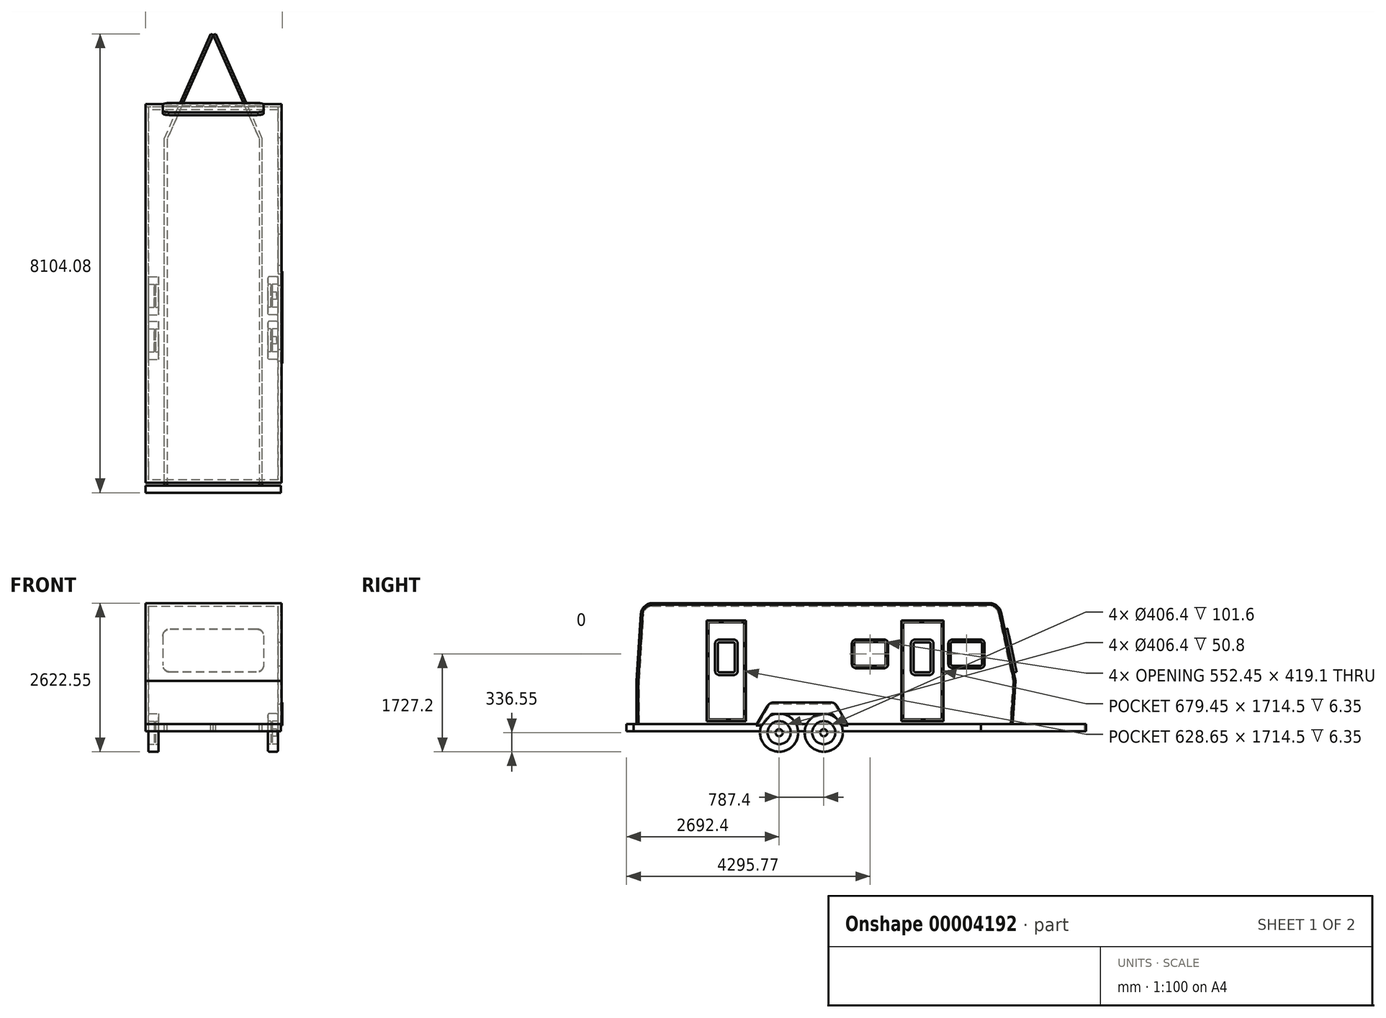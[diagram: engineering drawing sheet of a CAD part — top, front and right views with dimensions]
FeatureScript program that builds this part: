
annotation { "Feature Type Name" : "Feature", "Feature Type Description" : "" }
export const myFeature = defineFeature(function(context is Context, id is Id, definition is map)
    precondition{}
    {
        {
            var Q0;
            Q0=qCreatedBy(makeId("Right.planeOp"),FACE);
            var sketch = newSketch(context, id + "F0", { "sketchPlane" : qUnion([Q0])});
            skLineSegment(sketch, "E0", {"start": v(3587.75, 0) * mm, "end": v(-3048, 0) * mm});
            skLineSegment(sketch, "E1", {"start": v(-3048, 0) * mm, "end": v(-3048, 762) * mm});
            skLineSegment(sketch, "E2", {"start": v(-3048, 762) * mm, "end": v(-2971.8, 1943.48) * mm});
            skArc(sketch, "E3", {"start": v(-2971.8, 1943.48) * mm, "mid": v(-2908, 2078.64) * mm, "end": v(-2769.02, 2133.6) * mm});
            skLineSegment(sketch, "E4", {"start": v(-2769.02, 2133.6) * mm, "end": v(3181.35, 2133.6) * mm});
            skArc(sketch, "E5", {"start": v(3181.35, 2133.6) * mm, "mid": v(3309.16, 2088.37) * mm, "end": v(3380.07, 1972.82) * mm});
            skLineSegment(sketch, "E6", {"start": v(3380.07, 1972.82) * mm, "end": v(3638.55, 762) * mm});
            skLineSegment(sketch, "E7", {"start": v(3638.55, 762) * mm, "end": v(3587.75, 0) * mm});
            skLineSegment(sketch, "E8", {"start": v(2368.55, 0) * mm, "end": v(2368.55, 1879.6) * mm, "construction": true});
            skLineSegment(sketch, "E9", {"start": v(2368.55, 1879.6) * mm, "end": v(1689.1, 1879.6) * mm, "construction": true});
            skLineSegment(sketch, "E10", {"start": v(1689.1, 1879.6) * mm, "end": v(1689.1, 0) * mm, "construction": true});
            skLineSegment(sketch, "E11", {"start": v(-1149.35, 0) * mm, "end": v(-1149.35, 1879.6) * mm, "construction": true});
            skLineSegment(sketch, "E12", {"start": v(-1149.35, 1879.6) * mm, "end": v(-1778, 1879.6) * mm, "construction": true});
            skLineSegment(sketch, "E13", {"start": v(-1778, 1879.6) * mm, "end": v(-1778, 0) * mm, "construction": true});
            skLineSegment(sketch, "E14", {"start": v(-3048, 762) * mm, "end": v(-3048, 2133.6) * mm, "construction": true});
            skSolve(sketch);
        }
        {
            var Q0;
            Q0 = qSketchRegion(id + "F0", true);
            extrude(context, id + "F1", {"entities" : qUnion([Q0]), "endBound" : BoundingType.SYMMETRIC, "depth" : 2387.6 * mm});
        }
        {
            var Q0;
            Q0=makeQuery(id+"F1.opExtrude","SWEPT_FACE",FACE,{"disambiguationData":[OSD([sQuery(id+"F0.wireOp",EDGE,"E0")])]});
            shell(context, id + "F2", {"entities" : qUnion([Q0]), "thickness" : 50.8 * mm});
        }
        {
            var Q0;
            Q0=makeQuery(id+"F1.opExtrude","CAP_FACE",FACE,{"disambiguationData":[OSD([sQuery(id+"F0.wireOp",EDGE,"E0"),sQuery(id+"F0.wireOp",EDGE,"E1"),sQuery(id+"F0.wireOp",EDGE,"E2"),sQuery(id+"F0.wireOp",EDGE,"E3"),sQuery(id+"F0.wireOp",EDGE,"E4"),sQuery(id+"F0.wireOp",EDGE,"E5"),sQuery(id+"F0.wireOp",EDGE,"E6"),sQuery(id+"F0.wireOp",EDGE,"E7")])],"isStart":false});
            var sketch = newSketch(context, id + "F3", { "sketchPlane" : qUnion([Q0])});
            skLineSegment(sketch, "E15.bottom", {"start": v(2368.55, 1828.8) * mm, "end": v(1625.6, 1828.8) * mm});
            skLineSegment(sketch, "E15.top", {"start": v(2368.55, 50.8) * mm, "end": v(1625.6, 50.8) * mm});
            skLineSegment(sketch, "E15.left", {"start": v(2368.55, 1828.8) * mm, "end": v(2368.55, 50.8) * mm});
            skLineSegment(sketch, "E15.right", {"start": v(1625.6, 1828.8) * mm, "end": v(1625.6, 50.8) * mm});
            skLineSegment(sketch, "E16.bottom", {"start": v(-1117.6, 1828.8) * mm, "end": v(-1809.75, 1828.8) * mm});
            skLineSegment(sketch, "E16.top", {"start": v(-1117.6, 50.8) * mm, "end": v(-1809.75, 50.8) * mm});
            skLineSegment(sketch, "E16.left", {"start": v(-1117.6, 1828.8) * mm, "end": v(-1117.6, 50.8) * mm});
            skLineSegment(sketch, "E16.right", {"start": v(-1809.75, 1828.8) * mm, "end": v(-1809.75, 50.8) * mm});
            skLineSegment(sketch, "E17.bottom", {"start": v(-1149.35, 1797.05) * mm, "end": v(-1778, 1797.05) * mm});
            skLineSegment(sketch, "E17.top", {"start": v(-1149.35, 82.55) * mm, "end": v(-1778, 82.55) * mm});
            skLineSegment(sketch, "E17.left", {"start": v(-1149.35, 1797.05) * mm, "end": v(-1149.35, 82.55) * mm});
            skLineSegment(sketch, "E17.right", {"start": v(-1778, 1797.05) * mm, "end": v(-1778, 82.55) * mm});
            skLineSegment(sketch, "E18.bottom", {"start": v(2336.8, 1797.05) * mm, "end": v(1657.35, 1797.05) * mm});
            skLineSegment(sketch, "E18.top", {"start": v(2336.8, 82.55) * mm, "end": v(1657.35, 82.55) * mm});
            skLineSegment(sketch, "E18.left", {"start": v(2336.8, 1797.05) * mm, "end": v(2336.8, 82.55) * mm});
            skLineSegment(sketch, "E18.right", {"start": v(1657.35, 1797.05) * mm, "end": v(1657.35, 82.55) * mm});
            skSolve(sketch);
        }
        {
            var Q0;
            Q0 = qSketchRegion(id + "F3", true);
            extrude(context, id + "F4", {"entities" : qUnion([Q0]), "operationType" : NewBodyOperationType.ADD, "depth" : 6.35 * mm});
        }
        {
            var Q0;
            Q0=makeQuery(id+"F1.opExtrude","CAP_FACE",FACE,{"disambiguationData":[OSD([sQuery(id+"F0.wireOp",EDGE,"E0"),sQuery(id+"F0.wireOp",EDGE,"E1"),sQuery(id+"F0.wireOp",EDGE,"E2"),sQuery(id+"F0.wireOp",EDGE,"E3"),sQuery(id+"F0.wireOp",EDGE,"E4"),sQuery(id+"F0.wireOp",EDGE,"E5"),sQuery(id+"F0.wireOp",EDGE,"E6"),sQuery(id+"F0.wireOp",EDGE,"E7")])],"isStart":false});
            var sketch = newSketch(context, id + "F5", { "sketchPlane" : qUnion([Q0])});
            skLineSegment(sketch, "E19", {"start": v(-1263.65, 939.8) * mm, "end": v(-1263.65, 1416.05) * mm});
            skArc(sketch, "E20", {"start": v(-1263.65, 1416.05) * mm, "mid": v(-1285.97, 1469.93) * mm, "end": v(-1339.85, 1492.25) * mm});
            skLineSegment(sketch, "E21", {"start": v(-1339.85, 1492.25) * mm, "end": v(-1587.5, 1492.25) * mm});
            skArc(sketch, "E22", {"start": v(-1587.5, 1492.25) * mm, "mid": v(-1641.38, 1469.93) * mm, "end": v(-1663.7, 1416.05) * mm});
            skLineSegment(sketch, "E23", {"start": v(-1663.7, 1416.05) * mm, "end": v(-1663.7, 939.8) * mm});
            skArc(sketch, "E24", {"start": v(-1663.7, 939.8) * mm, "mid": v(-1641.38, 885.92) * mm, "end": v(-1587.5, 863.6) * mm});
            skLineSegment(sketch, "E25", {"start": v(-1587.5, 863.6) * mm, "end": v(-1339.85, 863.6) * mm});
            skArc(sketch, "E26", {"start": v(-1339.85, 863.6) * mm, "mid": v(-1285.97, 885.92) * mm, "end": v(-1263.65, 939.8) * mm});
            skArc(sketch, "E27.0", {"start": v(-1314.45, 1416.05) * mm, "mid": v(-1321.89, 1434.01) * mm, "end": v(-1339.85, 1441.45) * mm});
            skLineSegment(sketch, "E27.1", {"start": v(-1314.45, 939.8) * mm, "end": v(-1314.45, 1416.05) * mm});
            skLineSegment(sketch, "E27.2", {"start": v(-1339.85, 1441.45) * mm, "end": v(-1587.5, 1441.45) * mm});
            skArc(sketch, "E27.3", {"start": v(-1339.85, 914.4) * mm, "mid": v(-1321.89, 921.84) * mm, "end": v(-1314.45, 939.8) * mm});
            skArc(sketch, "E27.4", {"start": v(-1587.5, 1441.45) * mm, "mid": v(-1605.46, 1434.01) * mm, "end": v(-1612.9, 1416.05) * mm});
            skLineSegment(sketch, "E27.5", {"start": v(-1612.9, 1416.05) * mm, "end": v(-1612.9, 939.8) * mm});
            skArc(sketch, "E27.6", {"start": v(-1612.9, 939.8) * mm, "mid": v(-1605.46, 921.84) * mm, "end": v(-1587.5, 914.4) * mm});
            skLineSegment(sketch, "E27.7", {"start": v(-1587.5, 914.4) * mm, "end": v(-1339.85, 914.4) * mm});
            skSolve(sketch);
        }
        {
            var Q0;
            Q0 = qSketchRegion(id + "F5", true);
            extrude(context, id + "F6", {"entities" : qUnion([Q0]), "depth" : 12.7 * mm});
        }
        {
            var Q0;
            Q0=makeQuery(id+"F6.opExtrude","SWEPT_BODY",BODY,{"disambiguationData":[OSD([sQuery(id+"F5.wireOp",EDGE,"E19"),sQuery(id+"F5.wireOp",EDGE,"E20"),sQuery(id+"F5.wireOp",EDGE,"E21"),sQuery(id+"F5.wireOp",EDGE,"E22"),sQuery(id+"F5.wireOp",EDGE,"E23"),sQuery(id+"F5.wireOp",EDGE,"E24"),sQuery(id+"F5.wireOp",EDGE,"E25"),sQuery(id+"F5.wireOp",EDGE,"E26"),sQuery(id+"F5.wireOp",EDGE,"E27.0"),sQuery(id+"F5.wireOp",EDGE,"E27.1"),sQuery(id+"F5.wireOp",EDGE,"E27.2"),sQuery(id+"F5.wireOp",EDGE,"E27.3"),sQuery(id+"F5.wireOp",EDGE,"E27.4"),sQuery(id+"F5.wireOp",EDGE,"E27.5"),sQuery(id+"F5.wireOp",EDGE,"E27.6"),sQuery(id+"F5.wireOp",EDGE,"E27.7")])]});
            var Q1;
            Q1=makeQuery(id+"F1.opExtrude","CAP_EDGE",EDGE,{"disambiguationData":[OSD([sQuery(id+"F0.wireOp",EDGE,"E4")])],"isStart":false});
            transform(context, id + "F7", {"entities" : qUnion([Q0]), "transformType" : TransformType.TRANSLATION_DISTANCE, "transformDirection" : qUnion([Q1]), "distance" : 3454.4 * mm, "makeCopy" : true});
        }
        {
            var Q0;
            Q0=makeQuery(id+"F1.opExtrude","CAP_FACE",FACE,{"disambiguationData":[OSD([sQuery(id+"F0.wireOp",EDGE,"E0"),sQuery(id+"F0.wireOp",EDGE,"E1"),sQuery(id+"F0.wireOp",EDGE,"E2"),sQuery(id+"F0.wireOp",EDGE,"E3"),sQuery(id+"F0.wireOp",EDGE,"E4"),sQuery(id+"F0.wireOp",EDGE,"E5"),sQuery(id+"F0.wireOp",EDGE,"E6"),sQuery(id+"F0.wireOp",EDGE,"E7")])],"isStart":false});
            var sketch = newSketch(context, id + "F8", { "sketchPlane" : qUnion([Q0])});
            skLineSegment(sketch, "E28", {"start": v(3016.25, 1492.25) * mm, "end": v(2527.3, 1492.25) * mm});
            skArc(sketch, "E29", {"start": v(2527.3, 1492.25) * mm, "mid": v(2473.42, 1469.93) * mm, "end": v(2451.1, 1416.05) * mm});
            skLineSegment(sketch, "E30", {"start": v(2451.1, 1416.05) * mm, "end": v(2451.1, 1060.45) * mm});
            skArc(sketch, "E31", {"start": v(2451.1, 1060.45) * mm, "mid": v(2473.42, 1006.57) * mm, "end": v(2527.3, 984.25) * mm});
            skLineSegment(sketch, "E32", {"start": v(2527.3, 984.25) * mm, "end": v(3016.25, 984.25) * mm});
            skArc(sketch, "E33", {"start": v(3016.25, 984.25) * mm, "mid": v(3070.13, 1006.57) * mm, "end": v(3092.45, 1060.45) * mm});
            skLineSegment(sketch, "E34", {"start": v(3092.45, 1060.45) * mm, "end": v(3092.45, 1416.05) * mm});
            skArc(sketch, "E35", {"start": v(3092.45, 1416.05) * mm, "mid": v(3070.13, 1469.93) * mm, "end": v(3016.25, 1492.25) * mm});
            skArc(sketch, "E36.0", {"start": v(3048, 1416.05) * mm, "mid": v(3038.7, 1438.5) * mm, "end": v(3016.25, 1447.8) * mm});
            skLineSegment(sketch, "E36.1", {"start": v(3048, 1060.45) * mm, "end": v(3048, 1416.05) * mm});
            skLineSegment(sketch, "E36.2", {"start": v(3016.25, 1447.8) * mm, "end": v(2527.3, 1447.8) * mm});
            skArc(sketch, "E36.3", {"start": v(3016.25, 1028.7) * mm, "mid": v(3038.7, 1038) * mm, "end": v(3048, 1060.45) * mm});
            skArc(sketch, "E36.4", {"start": v(2527.3, 1447.8) * mm, "mid": v(2504.85, 1438.5) * mm, "end": v(2495.55, 1416.05) * mm});
            skLineSegment(sketch, "E36.5", {"start": v(2495.55, 1416.05) * mm, "end": v(2495.55, 1060.45) * mm});
            skArc(sketch, "E36.6", {"start": v(2495.55, 1060.45) * mm, "mid": v(2504.85, 1038) * mm, "end": v(2527.3, 1028.7) * mm});
            skLineSegment(sketch, "E36.7", {"start": v(2527.3, 1028.7) * mm, "end": v(3016.25, 1028.7) * mm});
            skSolve(sketch);
        }
        {
            var Q0;
            Q0 = qSketchRegion(id + "F8", true);
            extrude(context, id + "F9", {"entities" : qUnion([Q0]), "depth" : 6.35 * mm});
        }
        {
            var Q0;
            Q0=makeQuery(id+"F9.opExtrude","SWEPT_BODY",BODY,{"disambiguationData":[OSD([sQuery(id+"F8.wireOp",EDGE,"E28"),sQuery(id+"F8.wireOp",EDGE,"E29"),sQuery(id+"F8.wireOp",EDGE,"E30"),sQuery(id+"F8.wireOp",EDGE,"E31"),sQuery(id+"F8.wireOp",EDGE,"E32"),sQuery(id+"F8.wireOp",EDGE,"E33"),sQuery(id+"F8.wireOp",EDGE,"E34"),sQuery(id+"F8.wireOp",EDGE,"E35"),sQuery(id+"F8.wireOp",EDGE,"E36.0"),sQuery(id+"F8.wireOp",EDGE,"E36.1"),sQuery(id+"F8.wireOp",EDGE,"E36.2"),sQuery(id+"F8.wireOp",EDGE,"E36.3"),sQuery(id+"F8.wireOp",EDGE,"E36.4"),sQuery(id+"F8.wireOp",EDGE,"E36.5"),sQuery(id+"F8.wireOp",EDGE,"E36.6"),sQuery(id+"F8.wireOp",EDGE,"E36.7")])]});
            transform(context, id + "F10", {"entities" : qUnion([Q0]), "transformType" : TransformType.TRANSLATION_3D, "dx" : 0 * mm, "dy" : -1701.8 * mm, "dz" : 0 * mm, "makeCopy" : true});
        }
        {
            var Q0;
            Q0=makeQuery(id+"F1.opExtrude","CAP_FACE",FACE,{"disambiguationData":[OSD([sQuery(id+"F0.wireOp",EDGE,"E0"),sQuery(id+"F0.wireOp",EDGE,"E1"),sQuery(id+"F0.wireOp",EDGE,"E2"),sQuery(id+"F0.wireOp",EDGE,"E3"),sQuery(id+"F0.wireOp",EDGE,"E4"),sQuery(id+"F0.wireOp",EDGE,"E5"),sQuery(id+"F0.wireOp",EDGE,"E6"),sQuery(id+"F0.wireOp",EDGE,"E7")])],"isStart":false});
            var sketch = newSketch(context, id + "F11", { "sketchPlane" : qUnion([Q0])});
            skLineSegment(sketch, "E37", {"start": v(1314.45, 1447.8) * mm, "end": v(825.5, 1447.8) * mm});
            skArc(sketch, "E38", {"start": v(825.5, 1447.8) * mm, "mid": v(803.05, 1438.5) * mm, "end": v(793.75, 1416.05) * mm});
            skLineSegment(sketch, "E39", {"start": v(793.75, 1416.05) * mm, "end": v(793.75, 1060.45) * mm});
            skArc(sketch, "E40", {"start": v(793.75, 1060.45) * mm, "mid": v(803.05, 1038) * mm, "end": v(825.5, 1028.7) * mm});
            skLineSegment(sketch, "E41", {"start": v(825.5, 1028.7) * mm, "end": v(1314.45, 1028.7) * mm});
            skArc(sketch, "E42", {"start": v(1314.45, 1447.8) * mm, "mid": v(1336.9, 1438.5) * mm, "end": v(1346.2, 1416.05) * mm});
            skLineSegment(sketch, "E43", {"start": v(1346.2, 1416.05) * mm, "end": v(1346.2, 1060.45) * mm});
            skArc(sketch, "E44", {"start": v(1346.2, 1060.45) * mm, "mid": v(1336.9, 1038) * mm, "end": v(1314.45, 1028.7) * mm});
            skSolve(sketch);
        }
        {
            var Q0;
            Q0 = qSketchRegion(id + "F11", true);
            extrude(context, id + "F12", {"entities" : qUnion([Q0]), "operationType" : NewBodyOperationType.REMOVE, "oppositeDirection" : true, "depth" : 50.8 * mm});
        }
        {
            var Q0;
            Q0=qCreatedBy(makeId("Right.planeOp"),FACE);
            cPlane(context, id + "F13", {"entities" : qUnion([Q0]), "cplaneType" : CPlaneType.OFFSET, "offset" : 965.2 * mm, "width" : 152.4 * mm, "height" : 152.4 * mm});
        }
        {
            var Q0;
            Q0=qCreatedBy(id+"F13.planeOp",FACE);
            var sketch = newSketch(context, id + "F14", { "sketchPlane" : qUnion([Q0])});
            skCircle(sketch, "E45", {"center": v(-533.4, -152.4) * mm, "radius": 336.55 * mm});
            skCircle(sketch, "E46", {"center": v(-533.4, -152.4) * mm, "radius": 203.2 * mm});
            skCircle(sketch, "E47", {"center": v(254, -152.4) * mm, "radius": 336.55 * mm});
            skCircle(sketch, "E48", {"center": v(254, -152.4) * mm, "radius": 203.2 * mm});
            skSolve(sketch);
        }
        {
            var Q0;
            Q0 = qSketchRegion(id + "F14", true);
            extrude(context, id + "F15", {"entities" : qUnion([Q0]), "depth" : 177.8 * mm});
        }
        {
            var Q0;
            Q0=makeQuery(id+"F1.opExtrude","CAP_FACE",FACE,{"disambiguationData":[OSD([sQuery(id+"F0.wireOp",EDGE,"E0"),sQuery(id+"F0.wireOp",EDGE,"E1"),sQuery(id+"F0.wireOp",EDGE,"E2"),sQuery(id+"F0.wireOp",EDGE,"E3"),sQuery(id+"F0.wireOp",EDGE,"E4"),sQuery(id+"F0.wireOp",EDGE,"E5"),sQuery(id+"F0.wireOp",EDGE,"E6"),sQuery(id+"F0.wireOp",EDGE,"E7")])],"isStart":false});
            var sketch = newSketch(context, id + "F16", { "sketchPlane" : qUnion([Q0])});
            skLineSegment(sketch, "E49", {"start": v(-838.2, -25.4) * mm, "end": v(-939.8, -25.4) * mm});
            skLineSegment(sketch, "E50", {"start": v(-939.8, -25.4) * mm, "end": v(-705.16, 381) * mm});
            skLineSegment(sketch, "E51", {"start": v(-705.16, 381) * mm, "end": v(451.16, 381) * mm});
            skLineSegment(sketch, "E52", {"start": v(451.16, 381) * mm, "end": v(685.8, -25.4) * mm});
            skLineSegment(sketch, "E53", {"start": v(685.8, -25.4) * mm, "end": v(584.2, -25.4) * mm});
            skLineSegment(sketch, "E54", {"start": v(584.2, -25.4) * mm, "end": v(413.7, 177.8) * mm});
            skLineSegment(sketch, "E55", {"start": v(413.7, 177.8) * mm, "end": v(-667.7, 177.8) * mm});
            skLineSegment(sketch, "E56", {"start": v(-667.7, 177.8) * mm, "end": v(-838.2, -25.4) * mm});
            skSolve(sketch);
        }
        {
            var Q0;
            Q0 = qSketchRegion(id + "F16", true);
            extrude(context, id + "F17", {"entities" : qUnion([Q0]), "depth" : 25.4 * mm});
        }
        {
            var Q0;
            Q0=makeQuery(id+"F1.opExtrude","CAP_FACE",FACE,{"disambiguationData":[OSD([sQuery(id+"F0.wireOp",EDGE,"E0"),sQuery(id+"F0.wireOp",EDGE,"E1"),sQuery(id+"F0.wireOp",EDGE,"E2"),sQuery(id+"F0.wireOp",EDGE,"E3"),sQuery(id+"F0.wireOp",EDGE,"E4"),sQuery(id+"F0.wireOp",EDGE,"E5"),sQuery(id+"F0.wireOp",EDGE,"E6"),sQuery(id+"F0.wireOp",EDGE,"E7")])],"isStart":false});
            var sketch = newSketch(context, id + "F18", { "sketchPlane" : qUnion([Q0])});
            skLineSegment(sketch, "E57", {"start": v(-895.8, 0) * mm, "end": v(-690.5, 355.6) * mm});
            skLineSegment(sketch, "E58", {"start": v(-690.5, 355.6) * mm, "end": v(436.5, 355.6) * mm});
            skLineSegment(sketch, "E59", {"start": v(436.5, 355.6) * mm, "end": v(641.8, 0) * mm});
            skLineSegment(sketch, "E60", {"start": v(641.8, 0) * mm, "end": v(-895.8, 0) * mm});
            skSolve(sketch);
        }
        {
            var Q0;
            Q0 = qSketchRegion(id + "F18", true);
            extrude(context, id + "F19", {"entities" : qUnion([Q0]), "operationType" : NewBodyOperationType.REMOVE, "oppositeDirection" : true, "depth" : 50.8 * mm});
        }
        {
            var Q0;
            Q0=qCreatedBy(makeId("Top.planeOp"),FACE);
            var sketch = newSketch(context, id + "F20", { "sketchPlane" : qUnion([Q0])});
            skLineSegment(sketch, "E61", {"start": v(863.6, -3098.8) * mm, "end": v(863.6, 3028.95) * mm});
            skLineSegment(sketch, "E62", {"start": v(863.6, 3028.95) * mm, "end": v(46.47, 4878.28) * mm});
            skLineSegment(sketch, "E63", {"start": v(46.47, 4878.28) * mm, "end": v(0, 4857.75) * mm});
            skLineSegment(sketch, "E64", {"start": v(0, 4857.75) * mm, "end": v(812.8, 3018.23) * mm});
            skLineSegment(sketch, "E65", {"start": v(812.8, 3018.23) * mm, "end": v(812.8, -3098.8) * mm});
            skLineSegment(sketch, "E66", {"start": v(812.8, -3098.8) * mm, "end": v(863.6, -3098.8) * mm});
            skLineSegment(sketch, "E67.MirrorCS", {"start": v(-46.47, 4878.28) * mm, "end": v(0, 4857.75) * mm});
            skLineSegment(sketch, "E68.MirrorCS", {"start": v(-863.6, 3028.95) * mm, "end": v(-46.47, 4878.28) * mm});
            skLineSegment(sketch, "E69.MirrorCS", {"start": v(0, 4857.75) * mm, "end": v(-812.8, 3018.23) * mm});
            skLineSegment(sketch, "E70.MirrorCS", {"start": v(-863.6, -3098.8) * mm, "end": v(-863.6, 3028.95) * mm});
            skLineSegment(sketch, "E71.MirrorCS", {"start": v(-812.8, 3018.23) * mm, "end": v(-812.8, -3098.8) * mm});
            skLineSegment(sketch, "E72.MirrorCS", {"start": v(-812.8, -3098.8) * mm, "end": v(-863.6, -3098.8) * mm});
            skSolve(sketch);
        }
        {
            var Q0;
            Q0 = qSketchRegion(id + "F20", true);
            extrude(context, id + "F21", {"entities" : qUnion([Q0]), "oppositeDirection" : true, "depth" : 127 * mm});
        }
        {
            var Q0;
            Q0=makeQuery(id+"F15.opExtrude","CAP_FACE",FACE,{"disambiguationData":[OSD([sQuery(id+"F14.wireOp",EDGE,"E45"),sQuery(id+"F14.wireOp",EDGE,"E46")])],"isStart":true});
            cPlane(context, id + "F22", {"entities" : qUnion([Q0]), "cplaneType" : CPlaneType.OFFSET, "offset" : 50.8 * mm, "oppositeDirection" : true, "width" : 152.4 * mm, "height" : 152.4 * mm});
        }
        {
            var Q0;
            Q0=qCreatedBy(id+"F22.planeOp",FACE);
            var sketch = newSketch(context, id + "F23", { "sketchPlane" : qUnion([Q0])});
            skCircle(sketch, "E73", {"center": v(533.4, -152.4) * mm, "radius": 203.2 * mm});
            skCircle(sketch, "E74", {"center": v(-254, -152.4) * mm, "radius": 203.2 * mm});
            skSolve(sketch);
        }
        {
            var Q0;
            Q0 = qSketchRegion(id + "F23", true);
            extrude(context, id + "F24", {"entities" : qUnion([Q0]), "operationType" : NewBodyOperationType.ADD, "oppositeDirection" : true, "depth" : 25.4 * mm});
        }
        {
            var Q0;
            Q0=makeQuery(id+"F15.opExtrude","SWEPT_BODY",BODY,{"disambiguationData":[OSD([sQuery(id+"F14.wireOp",EDGE,"E47"),sQuery(id+"F14.wireOp",EDGE,"E48")])]});
            var Q1;
            Q1=makeQuery(id+"F15.opExtrude","SWEPT_BODY",BODY,{"disambiguationData":[OSD([sQuery(id+"F14.wireOp",EDGE,"E45"),sQuery(id+"F14.wireOp",EDGE,"E46")])]});
            var Q2;
            Q2=qCreatedBy(makeId("Right.planeOp"),FACE);
            mirror(context, id + "F25", {"operationType" : NewBodyOperationType.ADD, "entities" : qUnion([Q0, Q1]), "mirrorPlane" : qUnion([Q2])});
        }
        {
            var Q0;
            Q0=qCreatedBy(makeId("Right.planeOp"),FACE);
            var sketch = newSketch(context, id + "F26", { "sketchPlane" : qUnion([Q0])});
            skLineSegment(sketch, "E75.bottom", {"start": v(-3098.8, 0) * mm, "end": v(-3225.8, 0) * mm});
            skLineSegment(sketch, "E75.top", {"start": v(-3098.8, -127) * mm, "end": v(-3225.8, -127) * mm});
            skLineSegment(sketch, "E75.left", {"start": v(-3098.8, 0) * mm, "end": v(-3098.8, -127) * mm});
            skLineSegment(sketch, "E75.right", {"start": v(-3225.8, 0) * mm, "end": v(-3225.8, -127) * mm});
            skSolve(sketch);
        }
        {
            var Q0;
            Q0 = qSketchRegion(id + "F26", true);
            extrude(context, id + "F27", {"entities" : qUnion([Q0]), "endBound" : BoundingType.SYMMETRIC, "depth" : 2387.6 * mm});
        }
        {
            var Q0;
            Q0=makeQuery(id+"F1.opExtrude","SWEPT_FACE",FACE,{"disambiguationData":[OSD([sQuery(id+"F0.wireOp",EDGE,"E6")])]});
            var sketch = newSketch(context, id + "F28", { "sketchPlane" : qUnion([Q0])});
            skLineSegment(sketch, "E76", {"start": v(762, 918.9) * mm, "end": v(-762, 918.9) * mm});
            skArc(sketch, "E77", {"start": v(-762, 918.9) * mm, "mid": v(-851.8, 881.7) * mm, "end": v(-889, 791.9) * mm});
            skLineSegment(sketch, "E78", {"start": v(-889, 791.9) * mm, "end": v(-889, 265) * mm});
            skArc(sketch, "E79", {"start": v(-889, 265) * mm, "mid": v(-851.8, 175.2) * mm, "end": v(-762, 138) * mm});
            skLineSegment(sketch, "E80", {"start": v(-762, 138) * mm, "end": v(762, 138) * mm});
            skArc(sketch, "E81", {"start": v(762, 918.9) * mm, "mid": v(851.8, 881.7) * mm, "end": v(889, 791.9) * mm});
            skLineSegment(sketch, "E82", {"start": v(889, 791.9) * mm, "end": v(889, 265) * mm});
            skArc(sketch, "E83", {"start": v(889, 265) * mm, "mid": v(851.8, 175.2) * mm, "end": v(762, 138) * mm});
            skSolve(sketch);
        }
        {
            var Q0;
            Q0 = qSketchRegion(id + "F28", true);
            extrude(context, id + "F29", {"entities" : qUnion([Q0]), "operationType" : NewBodyOperationType.ADD, "depth" : 50.8 * mm});
        }
        {
            var Q0;
            Q0=makeQuery(id+"F24.opExtrude","CAP_FACE",FACE,{"disambiguationData":[OSD([sQuery(id+"F23.wireOp",EDGE,"E73")])],"isStart":false});
            var sketch = newSketch(context, id + "F30", { "sketchPlane" : qUnion([Q0])});
            skCircle(sketch, "E84", {"center": v(-533.4, -152.4) * mm, "radius": 63.5 * mm});
            skCircle(sketch, "E85", {"center": v(254, -152.4) * mm, "radius": 63.5 * mm});
            skSolve(sketch);
        }
        {
            var Q0;
            Q0 = qSketchRegion(id + "F30", true);
            extrude(context, id + "F31", {"entities" : qUnion([Q0]), "operationType" : NewBodyOperationType.ADD, "depth" : 76.2 * mm});
        }
        {
            var Q0;
            Q0=makeQuery(id+"F15.opExtrude","CAP_EDGE",EDGE,{"disambiguationData":[OSD([sQuery(id+"F14.wireOp",EDGE,"E45")])],"isStart":false});
            var Q1;
            Q1=makeQuery(id+"F15.opExtrude","CAP_EDGE",EDGE,{"disambiguationData":[OSD([sQuery(id+"F14.wireOp",EDGE,"E47")])],"isStart":false});
            var Q2;
            Q2=makeQuery(id+"F15.opExtrude","CAP_EDGE",EDGE,{"disambiguationData":[OSD([sQuery(id+"F14.wireOp",EDGE,"E45")])],"isStart":true});
            var Q3;
            Q3=makeQuery(id+"F15.opExtrude","CAP_EDGE",EDGE,{"disambiguationData":[OSD([sQuery(id+"F14.wireOp",EDGE,"E47")])],"isStart":true});
            fillet(context, id + "F32", {"entities" : qUnion([Q0, Q1, Q2, Q3]), "radius" : 25.4 * mm, "tangentPropagation" : true, "allowEdgeOverflow" : false});
        }
        {
            var Q0;
            Q0=makeQuery(id+"F1.opExtrude","CAP_FACE",FACE,{"disambiguationData":[OSD([sQuery(id+"F0.wireOp",EDGE,"E0"),sQuery(id+"F0.wireOp",EDGE,"E1"),sQuery(id+"F0.wireOp",EDGE,"E2"),sQuery(id+"F0.wireOp",EDGE,"E3"),sQuery(id+"F0.wireOp",EDGE,"E4"),sQuery(id+"F0.wireOp",EDGE,"E5"),sQuery(id+"F0.wireOp",EDGE,"E6"),sQuery(id+"F0.wireOp",EDGE,"E7")])],"isStart":false});
            var sketch = newSketch(context, id + "F33", { "sketchPlane" : qUnion([Q0])});
            skLineSegment(sketch, "E86", {"start": v(-3048, 0) * mm, "end": v(-3048, 762) * mm});
            skLineSegment(sketch, "E87", {"start": v(-3048, 762) * mm, "end": v(-2971.8, 1943.48) * mm});
            skArc(sketch, "E88", {"start": v(-2971.8, 1943.48) * mm, "mid": v(-2908, 2078.64) * mm, "end": v(-2769.02, 2133.6) * mm});
            skLineSegment(sketch, "E89", {"start": v(-2769.02, 2133.6) * mm, "end": v(3181.35, 2133.6) * mm});
            skArc(sketch, "E90", {"start": v(3181.35, 2133.6) * mm, "mid": v(3309.16, 2088.37) * mm, "end": v(3380.07, 1972.82) * mm});
            skLineSegment(sketch, "E91", {"start": v(3380.07, 1972.82) * mm, "end": v(3638.55, 762) * mm});
            skLineSegment(sketch, "E92", {"start": v(3638.55, 762) * mm, "end": v(3587.75, 0) * mm});
            skLineSegment(sketch, "E93.0", {"start": v(-3019.43, 761.08) * mm, "end": v(-2943.28, 1941.64) * mm});
            skLineSegment(sketch, "E93.1", {"start": v(-3019.43, 0) * mm, "end": v(-3019.43, 761.08) * mm});
            skArc(sketch, "E94.0", {"start": v(-2943.28, 1941.64) * mm, "mid": v(-2888.46, 2057.8) * mm, "end": v(-2769.02, 2105.03) * mm});
            skLineSegment(sketch, "E95.0", {"start": v(-2769.02, 2105.03) * mm, "end": v(3181.35, 2105.03) * mm});
            skArc(sketch, "E96.0", {"start": v(3181.35, 2105.03) * mm, "mid": v(3291.19, 2066.16) * mm, "end": v(3352.13, 1966.86) * mm});
            skLineSegment(sketch, "E97.0", {"start": v(3352.13, 1966.86) * mm, "end": v(3610.6, 756.03) * mm});
            skLineSegment(sketch, "E98.0", {"start": v(3610.04, 763.9) * mm, "end": v(3559.11, 0) * mm});
            skLineSegment(sketch, "E99", {"start": v(-3048, 0) * mm, "end": v(-3019.43, 0) * mm});
            skLineSegment(sketch, "E100", {"start": v(3559.11, 0) * mm, "end": v(3587.75, 0) * mm});
            skSolve(sketch);
        }
        {
            var Q0;
            Q0 = qSketchRegion(id + "F33", true);
            extrude(context, id + "F34", {"entities" : qUnion([Q0]), "operationType" : NewBodyOperationType.ADD, "depth" : 9.52 * mm});
        }
        {
            var Q0;
            {var subQ0=sQuery(id+"F0.wireOp",EDGE,"E7");var subQ1=sQuery(id+"F0.wireOp",EDGE,"E6");var subQ2=sQuery(id+"F0.wireOp",EDGE,"E1");var subQ3=sQuery(id+"F0.wireOp",EDGE,"E5");var subQ4=sQuery(id+"F0.wireOp",EDGE,"E4");var subQ5=sQuery(id+"F0.wireOp",EDGE,"E0");var subQ6=sQuery(id+"F0.wireOp",EDGE,"E2");var subQ7=sQuery(id+"F0.wireOp",EDGE,"E3");Q0=makeQuery(id+"F4.boolean.opBoolean","SPLIT",FACE,{"disambiguationData":[TD([makeQuery(id+"F1.opExtrude","SWEPT_FACE",FACE,{"disambiguationData":[OSD([subQ5])]})])],"derivedFrom":makeQuery(id+"F1.opExtrude","CAP_FACE",FACE,{"disambiguationData":[OSD([subQ5,subQ2,subQ6,subQ7,subQ4,subQ3,subQ1,subQ0])],"isStart":false})});}
            var sketch = newSketch(context, id + "F35", { "sketchPlane" : qUnion([Q0])});
            skLineSegment(sketch, "E101.bottom", {"start": v(-1149.35, 914.4) * mm, "end": v(1898.65, 914.4) * mm, "construction": true});
            skLineSegment(sketch, "E101.top", {"start": v(-1149.35, 2133.6) * mm, "end": v(1898.65, 2133.6) * mm, "construction": true});
            skLineSegment(sketch, "E101.left", {"start": v(-1149.35, 914.4) * mm, "end": v(-1149.35, 2133.6) * mm, "construction": true});
            skLineSegment(sketch, "E101.right", {"start": v(1898.65, 914.4) * mm, "end": v(1898.65, 2133.6) * mm, "construction": true});
            skLineSegment(sketch, "E102.bottom", {"start": v(-1149.35, 914.4) * mm, "end": v(1657.35, 914.4) * mm, "construction": true});
            skLineSegment(sketch, "E102.top", {"start": v(-1149.35, 0) * mm, "end": v(1657.35, 0) * mm, "construction": true});
            skLineSegment(sketch, "E102.left", {"start": v(-1149.35, 914.4) * mm, "end": v(-1149.35, 0) * mm, "construction": true});
            skLineSegment(sketch, "E102.right", {"start": v(1657.35, 914.4) * mm, "end": v(1657.35, 0) * mm, "construction": true});
            skLineSegment(sketch, "E103.bottom", {"start": v(-1778, 914.4) * mm, "end": v(-3048, 914.4) * mm, "construction": true});
            skLineSegment(sketch, "E103.top", {"start": v(-1778, 0) * mm, "end": v(-3048, 0) * mm, "construction": true});
            skLineSegment(sketch, "E103.left", {"start": v(-1778, 914.4) * mm, "end": v(-1778, 0) * mm, "construction": true});
            skLineSegment(sketch, "E103.right", {"start": v(-3048, 914.4) * mm, "end": v(-3048, 0) * mm, "construction": true});
            skLineSegment(sketch, "E104.bottom", {"start": v(2336.8, 914.4) * mm, "end": v(3632.2, 914.4) * mm, "construction": true});
            skLineSegment(sketch, "E104.top", {"start": v(2336.8, 0) * mm, "end": v(3632.2, 0) * mm, "construction": true});
            skLineSegment(sketch, "E104.left", {"start": v(2336.8, 914.4) * mm, "end": v(2336.8, 0) * mm, "construction": true});
            skLineSegment(sketch, "E104.right", {"start": v(3632.2, 914.4) * mm, "end": v(3632.2, 0) * mm, "construction": true});
            skLineSegment(sketch, "E105.bottom", {"start": v(1898.65, 914.4) * mm, "end": v(3632.2, 914.4) * mm, "construction": true});
            skLineSegment(sketch, "E105.top", {"start": v(1898.65, 2133.6) * mm, "end": v(3346.45, 2133.6) * mm, "construction": true});
            skLineSegment(sketch, "E106.bottom", {"start": v(-1168.4, 2133.6) * mm, "end": v(-3048, 2133.6) * mm, "construction": true});
            skLineSegment(sketch, "E106.top", {"start": v(-1168.4, 914.4) * mm, "end": v(-3048, 914.4) * mm, "construction": true});
            skLineSegment(sketch, "E106.left", {"start": v(-1168.4, 2133.6) * mm, "end": v(-1168.4, 914.4) * mm, "construction": true});
            skLineSegment(sketch, "E106.right", {"start": v(-3048, 2133.6) * mm, "end": v(-3048, 914.4) * mm, "construction": true});
            skLineSegment(sketch, "E107", {"start": v(3632.2, 914.4) * mm, "end": v(3346.45, 2133.6) * mm, "construction": true});
            skLineSegment(sketch, "E108", {"start": v(3632.2, 914.4) * mm, "end": v(5080, 914.4) * mm, "construction": true});
            skLineSegment(sketch, "E109", {"start": v(3346.45, 2133.6) * mm, "end": v(5080, 2133.6) * mm, "construction": true});
            skLineSegment(sketch, "E110", {"start": v(5080, 2133.6) * mm, "end": v(5080, 914.4) * mm, "construction": true});
            skSolve(sketch);
        }
        {
            var Q0;
            Q0=makeQuery(id+"F35.imprint","IMPRINT",FACE,{"disambiguationData":[TD([[makeQuery(id+"F35.imprint","IMPRINT",EDGE,{"derivedFrom":makeQuery(id+"F4.opExtrude","CAP_EDGE",EDGE,{"disambiguationData":[OSD([sQuery(id+"F3.wireOp",EDGE,"E15.bottom")])],"isStart":true})}),-1.0]])]});
            var sketch = newSketch(context, id + "F36", { "sketchPlane" : qUnion([Q0])});
            skLineSegment(sketch, "E111", {"start": v(2527.3, 1447.8) * mm, "end": v(3016.25, 1447.8) * mm});
            skArc(sketch, "E112", {"start": v(3016.25, 1447.8) * mm, "mid": v(3038.7, 1438.5) * mm, "end": v(3048, 1416.05) * mm});
            skLineSegment(sketch, "E113", {"start": v(3048, 1416.05) * mm, "end": v(3048, 1060.45) * mm});
            skArc(sketch, "E114", {"start": v(3048, 1060.45) * mm, "mid": v(3038.7, 1038) * mm, "end": v(3016.25, 1028.7) * mm});
            skLineSegment(sketch, "E115", {"start": v(3016.25, 1028.7) * mm, "end": v(2527.3, 1028.7) * mm});
            skArc(sketch, "E116", {"start": v(2527.3, 1447.8) * mm, "mid": v(2504.85, 1438.5) * mm, "end": v(2495.55, 1416.05) * mm});
            skArc(sketch, "E117", {"start": v(2527.3, 1028.7) * mm, "mid": v(2504.85, 1038) * mm, "end": v(2495.55, 1060.45) * mm});
            skLineSegment(sketch, "E118", {"start": v(2495.55, 1416.05) * mm, "end": v(2495.55, 1060.45) * mm});
            skSolve(sketch);
        }
        {
            var Q0;
            Q0 = qSketchRegion(id + "F36", true);
            extrude(context, id + "F37", {"entities" : qUnion([Q0]), "operationType" : NewBodyOperationType.REMOVE, "oppositeDirection" : true, "depth" : 50.8 * mm});
        }
        {
            var Q0;
            Q0=makeQuery(id+"F17.opExtrude","SWEPT_EDGE",EDGE,{"disambiguationData":[OSD([sQuery(id+"F16.wireOp",EDGE,"E50"),sQuery(id+"F16.wireOp",EDGE,"E51")])]});
            var Q1;
            Q1=makeQuery(id+"F17.opExtrude","SWEPT_EDGE",EDGE,{"disambiguationData":[OSD([sQuery(id+"F16.wireOp",EDGE,"E51"),sQuery(id+"F16.wireOp",EDGE,"E52")])]});
            fillet(context, id + "F38", {"entities" : qUnion([Q0, Q1]), "radius" : 127 * mm, "tangentPropagation" : true, "allowEdgeOverflow" : false});
        }
    });
